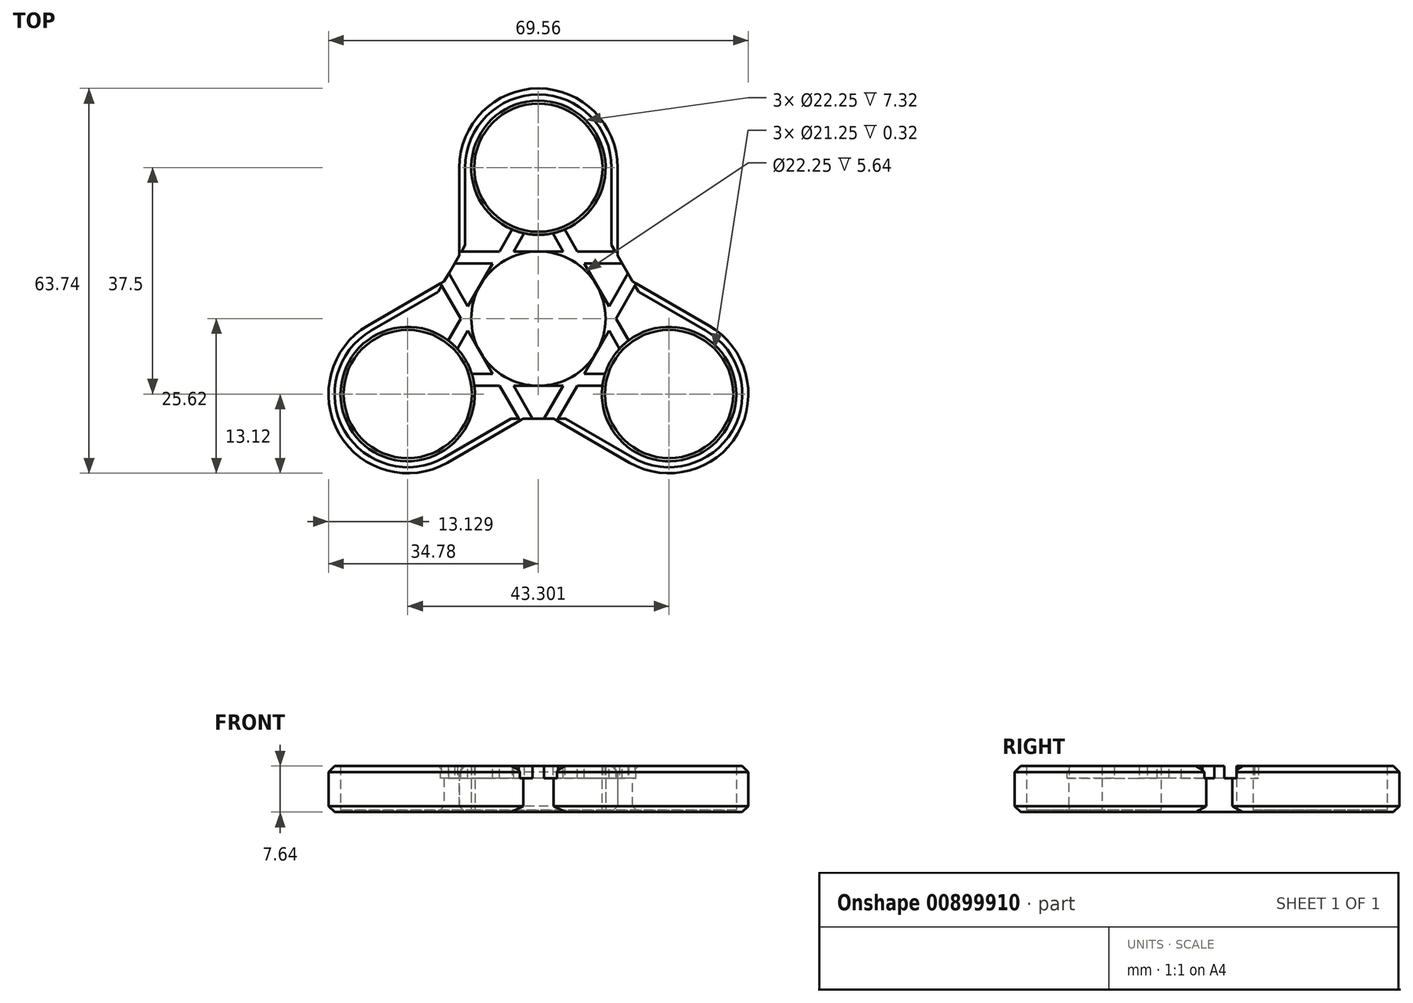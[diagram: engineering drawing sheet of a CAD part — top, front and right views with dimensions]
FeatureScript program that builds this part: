
annotation { "Feature Type Name" : "Feature", "Feature Type Description" : "" }
export const myFeature = defineFeature(function(context is Context, id is Id, definition is map)
    precondition{}
    {
        {
            var Q0;
            Q0=qCreatedBy(makeId("Top.planeOp"),FACE);
            var sketch = newSketch(context, id + "F0", { "sketchPlane" : qUnion([Q0])});
            skCircle(sketch, "E0", {"center": v(0, 0) * mm, "radius": 11.12 * mm});
            skCircle(sketch, "E1", {"center": v(0, 25) * mm, "radius": 11.12 * mm});
            skCircle(sketch, "E2", {"center": v(0, 25) * mm, "radius": 13.12 * mm});
            skCircle(sketch, "E3", {"center": v(0, 0) * mm, "radius": 13.12 * mm});
            skLineSegment(sketch, "E4", {"start": v(-13.12, 0) * mm, "end": v(-13.12, 25) * mm});
            skLineSegment(sketch, "E5", {"start": v(13.12, 0) * mm, "end": v(13.12, 25) * mm});
            skCircle(sketch, "E6.1.0", {"center": v(-21.65, -12.5) * mm, "radius": 11.12 * mm});
            skCircle(sketch, "E6.1.1", {"center": v(-21.65, -12.5) * mm, "radius": 13.12 * mm});
            skLineSegment(sketch, "E6.1.2", {"start": v(6.56, -11.37) * mm, "end": v(-15.09, -23.87) * mm});
            skLineSegment(sketch, "E6.1.3", {"start": v(-6.56, 11.37) * mm, "end": v(-28.21, -1.13) * mm});
            skCircle(sketch, "E6.2.0", {"center": v(21.65, -12.5) * mm, "radius": 11.12 * mm});
            skCircle(sketch, "E6.2.1", {"center": v(21.65, -12.5) * mm, "radius": 13.12 * mm});
            skLineSegment(sketch, "E6.2.2", {"start": v(6.56, 11.37) * mm, "end": v(28.21, -1.13) * mm});
            skLineSegment(sketch, "E6.2.3", {"start": v(-6.56, -11.37) * mm, "end": v(15.09, -23.87) * mm});
            skSolve(sketch);
        }
        {
            var Q0;
            Q0=makeQuery(id+"F0.imprint","IMPRINT",FACE,{"disambiguationData":[TD([[makeQuery(id+"F0.imprint","IMPRINT",EDGE,{"derivedFrom":sQuery(id+"F0.wireOp",EDGE,"E1")}),-1.0]])]});
            var Q1;
            {var subQ0=sQuery(id+"F0.wireOp",EDGE,"E4");var subQ1=sQuery(id+"F0.wireOp",EDGE,"E2");var subQ2=makeQuery(id+"F0.imprint","INTERSECT",VERTEX,{"derivedFrom":[subQ1,subQ0]});Q1=makeQuery(id+"F0.imprint","IMPRINT",FACE,{"disambiguationData":[TD([[makeQuery(id+"F0.imprint","IMPRINT",EDGE,{"disambiguationData":[TD([[subQ2,-1.0]])],"derivedFrom":subQ1}),-1.0]])]});}
            var Q2;
            {var subQ5=sQuery(id+"F0.wireOp",EDGE,"E4");var subQ6=sQuery(id+"F0.wireOp",EDGE,"E3");var subQ7=makeQuery(id+"F0.imprint","INTERSECT",VERTEX,{"derivedFrom":[subQ6,subQ5]});Q2=makeQuery(id+"F0.imprint","IMPRINT",FACE,{"disambiguationData":[TD([[makeQuery(id+"F0.imprint","IMPRINT",EDGE,{"disambiguationData":[TD([[subQ7,-1.0]])],"derivedFrom":subQ6}),-1.0]])]});}
            var Q3;
            Q3=makeQuery(id+"F0.imprint","IMPRINT",FACE,{"disambiguationData":[TD([[makeQuery(id+"F0.imprint","IMPRINT",EDGE,{"derivedFrom":sQuery(id+"F0.wireOp",EDGE,"E6.1.0")}),-1.0]])]});
            var Q4;
            {var subQ5=sQuery(id+"F0.wireOp",EDGE,"E5");var subQ6=sQuery(id+"F0.wireOp",EDGE,"E3");var subQ7=makeQuery(id+"F0.imprint","INTERSECT",VERTEX,{"derivedFrom":[subQ6,subQ5]});Q4=makeQuery(id+"F0.imprint","IMPRINT",FACE,{"disambiguationData":[TD([[makeQuery(id+"F0.imprint","IMPRINT",EDGE,{"disambiguationData":[TD([[subQ7,1.0]])],"derivedFrom":subQ6}),-1.0]])]});}
            var Q5;
            Q5=makeQuery(id+"F0.imprint","IMPRINT",FACE,{"disambiguationData":[TD([[makeQuery(id+"F0.imprint","IMPRINT",EDGE,{"derivedFrom":sQuery(id+"F0.wireOp",EDGE,"E6.2.0")}),-1.0]])]});
            var Q6;
            {var subQ0=sQuery(id+"F0.wireOp",EDGE,"E5");var subQ1=sQuery(id+"F0.wireOp",EDGE,"E3");var subQ2=makeQuery(id+"F0.imprint","INTERSECT",VERTEX,{"derivedFrom":[subQ1,subQ0]});Q6=makeQuery(id+"F0.imprint","IMPRINT",FACE,{"disambiguationData":[TD([[makeQuery(id+"F0.imprint","IMPRINT",EDGE,{"disambiguationData":[TD([[subQ2,-1.0]])],"derivedFrom":subQ1}),-1.0]])]});}
            var Q7;
            {var subQ0=sQuery(id+"F0.wireOp",EDGE,"E6.1.2");var subQ1=sQuery(id+"F0.wireOp",EDGE,"E3");var subQ2=makeQuery(id+"F0.imprint","INTERSECT",VERTEX,{"derivedFrom":[subQ1,subQ0]});Q7=makeQuery(id+"F0.imprint","IMPRINT",FACE,{"disambiguationData":[TD([[makeQuery(id+"F0.imprint","IMPRINT",EDGE,{"disambiguationData":[TD([[subQ2,1.0]])],"derivedFrom":subQ1}),-1.0]])]});}
            var Q8;
            {var subQ0=sQuery(id+"F0.wireOp",EDGE,"E4");var subQ1=sQuery(id+"F0.wireOp",EDGE,"E3");var subQ2=makeQuery(id+"F0.imprint","INTERSECT",VERTEX,{"derivedFrom":[subQ1,subQ0]});Q8=makeQuery(id+"F0.imprint","IMPRINT",FACE,{"disambiguationData":[TD([[makeQuery(id+"F0.imprint","IMPRINT",EDGE,{"disambiguationData":[TD([[subQ2,1.0]])],"derivedFrom":subQ1}),-1.0]])]});}
            var Q9;
            Q9=makeQuery(id+"F0.imprint","IMPRINT",FACE,{"disambiguationData":[TD([[makeQuery(id+"F0.imprint","IMPRINT",EDGE,{"derivedFrom":sQuery(id+"F0.wireOp",EDGE,"E0")}),-1.0]])]});
            var Q10;
            {var subQ0=sQuery(id+"F0.wireOp",EDGE,"E5");var subQ1=sQuery(id+"F0.wireOp",EDGE,"E2");var subQ2=makeQuery(id+"F0.imprint","INTERSECT",VERTEX,{"derivedFrom":[subQ1,subQ0]});Q10=makeQuery(id+"F0.imprint","IMPRINT",FACE,{"disambiguationData":[TD([[makeQuery(id+"F0.imprint","IMPRINT",EDGE,{"disambiguationData":[TD([[subQ2,1.0]])],"derivedFrom":subQ1}),-1.0]])]});}
            var Q11;
            {var subQ0=sQuery(id+"F0.wireOp",EDGE,"E6.1.2");var subQ1=sQuery(id+"F0.wireOp",EDGE,"E3");var subQ2=makeQuery(id+"F0.imprint","INTERSECT",VERTEX,{"derivedFrom":[subQ1,subQ0]});Q11=makeQuery(id+"F0.imprint","IMPRINT",FACE,{"disambiguationData":[TD([[makeQuery(id+"F0.imprint","IMPRINT",EDGE,{"disambiguationData":[TD([[subQ2,-1.0]])],"derivedFrom":subQ1}),-1.0]])]});}
            var Q12;
            {var subQ0=sQuery(id+"F0.wireOp",EDGE,"E6.2.3");var subQ1=sQuery(id+"F0.wireOp",EDGE,"E3");var subQ2=makeQuery(id+"F0.imprint","INTERSECT",VERTEX,{"derivedFrom":[subQ1,subQ0]});Q12=makeQuery(id+"F0.imprint","IMPRINT",FACE,{"disambiguationData":[TD([[makeQuery(id+"F0.imprint","IMPRINT",EDGE,{"disambiguationData":[TD([[subQ2,1.0]])],"derivedFrom":subQ1}),-1.0]])]});}
            var Q13;
            {var subQ0=sQuery(id+"F0.wireOp",EDGE,"E6.2.1");var subQ1=sQuery(id+"F0.wireOp",EDGE,"E3");var subQ2=makeQuery(id+"F0.imprint","INTERSECT",VERTEX,{"disambiguationData":[OD(0.0)],"derivedFrom":[subQ1,subQ0]});Q13=makeQuery(id+"F0.imprint","IMPRINT",FACE,{"disambiguationData":[TD([[makeQuery(id+"F0.imprint","IMPRINT",EDGE,{"disambiguationData":[TD([[subQ2,-1.0]])],"derivedFrom":subQ1}),1.0]])]});}
            var Q14;
            {var subQ0=sQuery(id+"F0.wireOp",EDGE,"E3");var subQ1=sQuery(id+"F0.wireOp",EDGE,"E2");var subQ2=makeQuery(id+"F0.imprint","INTERSECT",VERTEX,{"disambiguationData":[OD(0.0)],"derivedFrom":[subQ1,subQ0]});Q14=makeQuery(id+"F0.imprint","IMPRINT",FACE,{"disambiguationData":[TD([[makeQuery(id+"F0.imprint","IMPRINT",EDGE,{"disambiguationData":[TD([[subQ2,-1.0]])],"derivedFrom":subQ1}),1.0]])]});}
            var Q15;
            {var subQ0=sQuery(id+"F0.wireOp",EDGE,"E6.1.1");var subQ1=sQuery(id+"F0.wireOp",EDGE,"E3");var subQ2=makeQuery(id+"F0.imprint","INTERSECT",VERTEX,{"disambiguationData":[OD(0.0)],"derivedFrom":[subQ1,subQ0]});Q15=makeQuery(id+"F0.imprint","IMPRINT",FACE,{"disambiguationData":[TD([[makeQuery(id+"F0.imprint","IMPRINT",EDGE,{"disambiguationData":[TD([[subQ2,-1.0]])],"derivedFrom":subQ1}),1.0]])]});}
            extrude(context, id + "F1", {"entities" : qUnion([Q0, Q1, Q2, Q3, Q4, Q5, Q6, Q7, Q8, Q9, Q10, Q11, Q12, Q13, Q14, Q15]), "endBound" : BoundingType.SYMMETRIC, "depth" : 7.64 * mm, "offsetDistance" : 25 * mm});
        }
        {
            var Q0;
            Q0=makeQuery(id+"F1.opExtrude","CAP_FACE",FACE,{"disambiguationData":[OSD([sQuery(id+"F0.wireOp",EDGE,"E0"),sQuery(id+"F0.wireOp",EDGE,"E1"),sQuery(id+"F0.wireOp",EDGE,"E2"),sQuery(id+"F0.wireOp",EDGE,"E4"),sQuery(id+"F0.wireOp",EDGE,"E5"),sQuery(id+"F0.wireOp",EDGE,"E6.1.0"),sQuery(id+"F0.wireOp",EDGE,"E6.1.1"),sQuery(id+"F0.wireOp",EDGE,"E6.1.2"),sQuery(id+"F0.wireOp",EDGE,"E6.1.3"),sQuery(id+"F0.wireOp",EDGE,"E6.2.0"),sQuery(id+"F0.wireOp",EDGE,"E6.2.1"),sQuery(id+"F0.wireOp",EDGE,"E6.2.2"),sQuery(id+"F0.wireOp",EDGE,"E6.2.3")])],"isStart":false});
            var sketch = newSketch(context, id + "F2", { "sketchPlane" : qUnion([Q0])});
            skCircle(sketch, "E7.cCircle", {"center": v(0, 0) * mm, "radius": 11.12 * mm, "construction": true});
            skLineSegment(sketch, "E7.0", {"start": v(-19.27, 11.12) * mm, "end": v(19.27, 11.13) * mm});
            skLineSegment(sketch, "E7.1", {"start": v(19.27, 11.13) * mm, "end": v(0, -22.25) * mm});
            skLineSegment(sketch, "E7.2", {"start": v(0, -22.25) * mm, "end": v(-19.27, 11.13) * mm});
            skPoint(sketch, "E7.0.midPoint", {"position": v(0, 11.12) * mm});
            skLineSegment(sketch, "E8.0", {"start": v(0.09, 22.1) * mm, "end": v(19.18, -10.98) * mm});
            skLineSegment(sketch, "E8.1", {"start": v(19.1, -11.13) * mm, "end": v(-19.1, -11.12) * mm});
            skLineSegment(sketch, "E8.2", {"start": v(-19.18, -10.98) * mm, "end": v(-0.09, 22.1) * mm});
            skPoint(sketch, "E8.0.midPoint", {"position": v(9.63, 5.56) * mm});
            skLineSegment(sketch, "E9.0", {"start": v(0, 18.25) * mm, "end": v(15.8, -9.13) * mm});
            skLineSegment(sketch, "E9.1", {"start": v(-15.8, -9.13) * mm, "end": v(0, 18.25) * mm});
            skLineSegment(sketch, "E9.2", {"start": v(15.8, -9.13) * mm, "end": v(-15.8, -9.12) * mm});
            skLineSegment(sketch, "E10.0", {"start": v(15.8, 9.13) * mm, "end": v(0, -18.25) * mm});
            skLineSegment(sketch, "E10.1", {"start": v(-15.8, 9.12) * mm, "end": v(15.8, 9.12) * mm});
            skLineSegment(sketch, "E10.2", {"start": v(0, -18.25) * mm, "end": v(-15.8, 9.13) * mm});
            skPoint(sketch, "E11.visualSharp", {"position": v(19.27, -11.13) * mm});
            skArc(sketch, "E11.filletArc", {"start": v(19.1, -11.13) * mm, "mid": v(19.18, -11.08) * mm, "end": v(19.18, -10.98) * mm});
            skPoint(sketch, "E12.visualSharp", {"position": v(-19.27, -11.12) * mm});
            skArc(sketch, "E12.filletArc", {"start": v(-19.18, -10.97) * mm, "mid": v(-19.18, -11.07) * mm, "end": v(-19.1, -11.12) * mm});
            skPoint(sketch, "E13.visualSharp", {"position": v(0, 22.25) * mm});
            skArc(sketch, "E13.filletArc", {"start": v(0.09, 22.1) * mm, "mid": v(0, 22.15) * mm, "end": v(-0.09, 22.1) * mm});
            skSolve(sketch);
        }
        {
            var Q0;
            Q0=makeQuery(id+"F1.opExtrude","CAP_FACE",FACE,{"disambiguationData":[OSD([sQuery(id+"F0.wireOp",EDGE,"E0"),sQuery(id+"F0.wireOp",EDGE,"E1"),sQuery(id+"F0.wireOp",EDGE,"E2"),sQuery(id+"F0.wireOp",EDGE,"E4"),sQuery(id+"F0.wireOp",EDGE,"E5"),sQuery(id+"F0.wireOp",EDGE,"E6.1.0"),sQuery(id+"F0.wireOp",EDGE,"E6.1.1"),sQuery(id+"F0.wireOp",EDGE,"E6.1.2"),sQuery(id+"F0.wireOp",EDGE,"E6.1.3"),sQuery(id+"F0.wireOp",EDGE,"E6.2.0"),sQuery(id+"F0.wireOp",EDGE,"E6.2.1"),sQuery(id+"F0.wireOp",EDGE,"E6.2.2"),sQuery(id+"F0.wireOp",EDGE,"E6.2.3")])],"isStart":false});
            var sketch = newSketch(context, id + "F3", { "sketchPlane" : qUnion([Q0])});
            skArc(sketch, "E14.0", {"start": v(13.12, 25) * mm, "mid": v(0, 38.12) * mm, "end": v(-13.12, 25) * mm});
            skCircle(sketch, "E15.cCircle", {"center": v(0, 25) * mm, "radius": 13.12 * mm, "construction": true});
            skLineSegment(sketch, "E15.0", {"start": v(13.12, 32.58) * mm, "end": v(13.12, 17.42) * mm});
            skLineSegment(sketch, "E15.1", {"start": v(13.13, 17.42) * mm, "end": v(0, 9.84) * mm});
            skLineSegment(sketch, "E15.2", {"start": v(0, 9.84) * mm, "end": v(-13.13, 17.42) * mm});
            skLineSegment(sketch, "E15.3", {"start": v(-13.13, 17.42) * mm, "end": v(-13.13, 32.58) * mm});
            skLineSegment(sketch, "E15.4", {"start": v(-13.13, 32.58) * mm, "end": v(0, 40.16) * mm});
            skLineSegment(sketch, "E15.5", {"start": v(0, 40.16) * mm, "end": v(13.12, 32.58) * mm});
            skPoint(sketch, "E15.0.midPoint", {"position": v(13.12, 25) * mm});
            skSolve(sketch);
        }
        {
            var Q0;
            Q0=makeQuery(id+"F1.opExtrude","SWEPT_EDGE",EDGE,{"disambiguationData":[OSD([sQuery(id+"F0.wireOp",EDGE,"E5"),sQuery(id+"F0.wireOp",EDGE,"E6.2.2")])]});
            var Q1;
            Q1=makeQuery(id+"F1.opExtrude","SWEPT_EDGE",EDGE,{"disambiguationData":[OSD([sQuery(id+"F0.wireOp",EDGE,"E4"),sQuery(id+"F0.wireOp",EDGE,"E6.1.3")])]});
            var Q2;
            Q2=makeQuery(id+"F1.opExtrude","SWEPT_EDGE",EDGE,{"disambiguationData":[OSD([sQuery(id+"F0.wireOp",EDGE,"E6.1.2"),sQuery(id+"F0.wireOp",EDGE,"E6.2.3")])]});
            chamfer(context, id + "F4", {"entities" : qUnion([Q0, Q1, Q2]), "width" : 5 * mm, "tangentPropagation" : true});
        }
        {
            var Q0;
            Q0=makeQuery(id+"F1.opExtrude","CAP_EDGE",EDGE,{"disambiguationData":[OSD([sQuery(id+"F0.wireOp",EDGE,"E5")])],"isStart":false});
            var Q1;
            Q1=makeQuery(id+"F1.opExtrude","CAP_EDGE",EDGE,{"disambiguationData":[OSD([sQuery(id+"F0.wireOp",EDGE,"E6.2.3")])],"isStart":false});
            var Q2;
            Q2=makeQuery(id+"F1.opExtrude","CAP_EDGE",EDGE,{"disambiguationData":[OSD([sQuery(id+"F0.wireOp",EDGE,"E6.1.3")])],"isStart":false});
            chamfer(context, id + "F5", {"entities" : qUnion([Q0, Q1, Q2]), "width" : 1 * mm, "tangentPropagation" : true});
        }
        {
            var Q0;
            {var subQ0=sQuery(id+"F2.wireOp",EDGE,"E8.2");var subQ12=sQuery(id+"F2.wireOp",EDGE,"E7.2");var subQ13=makeQuery(id+"F2.imprint","INTERSECT",VERTEX,{"derivedFrom":[subQ12,subQ0]});Q0=makeQuery(id+"F2.imprint","IMPRINT",FACE,{"disambiguationData":[TD([[makeQuery(id+"F2.imprint","IMPRINT",EDGE,{"disambiguationData":[TD([[subQ13,-1.0]])],"derivedFrom":subQ0}),1.0]])]});}
            var Q1;
            {var subQ0=sQuery(id+"F2.wireOp",EDGE,"E8.2");var subQ1=sQuery(id+"F2.wireOp",EDGE,"E7.0");var subQ2=makeQuery(id+"F2.imprint","INTERSECT",VERTEX,{"derivedFrom":[subQ1,subQ0]});Q1=makeQuery(id+"F2.imprint","IMPRINT",FACE,{"disambiguationData":[TD([[makeQuery(id+"F2.imprint","IMPRINT",EDGE,{"disambiguationData":[TD([[subQ2,-1.0]])],"derivedFrom":subQ1}),1.0]])]});}
            var Q2;
            {var subQ0=sQuery(id+"F2.wireOp",EDGE,"E8.0");var subQ9=sQuery(id+"F2.wireOp",EDGE,"E7.0");var subQ10=makeQuery(id+"F2.imprint","INTERSECT",VERTEX,{"derivedFrom":[subQ9,subQ0]});Q2=makeQuery(id+"F2.imprint","IMPRINT",FACE,{"disambiguationData":[TD([[makeQuery(id+"F2.imprint","IMPRINT",EDGE,{"disambiguationData":[TD([[subQ10,-1.0]])],"derivedFrom":subQ0}),1.0]])]});}
            var Q3;
            {var subQ1=sQuery(id+"F2.wireOp",EDGE,"E7.1");var subQ7=sQuery(id+"F2.wireOp",EDGE,"E8.0");var subQ8=makeQuery(id+"F2.imprint","INTERSECT",VERTEX,{"derivedFrom":[subQ1,subQ7]});Q3=makeQuery(id+"F2.imprint","IMPRINT",FACE,{"disambiguationData":[TD([[makeQuery(id+"F2.imprint","IMPRINT",EDGE,{"disambiguationData":[TD([[subQ8,-1.0]])],"derivedFrom":subQ1}),1.0]])]});}
            var Q4;
            {var subQ0=sQuery(id+"F2.wireOp",EDGE,"E8.1");var subQ11=sQuery(id+"F2.wireOp",EDGE,"E7.1");var subQ12=makeQuery(id+"F2.imprint","INTERSECT",VERTEX,{"derivedFrom":[subQ11,subQ0]});Q4=makeQuery(id+"F2.imprint","IMPRINT",FACE,{"disambiguationData":[TD([[makeQuery(id+"F2.imprint","IMPRINT",EDGE,{"disambiguationData":[TD([[subQ12,-1.0]])],"derivedFrom":subQ0}),1.0]])]});}
            var Q5;
            {var subQ1=sQuery(id+"F2.wireOp",EDGE,"E7.2");var subQ7=sQuery(id+"F2.wireOp",EDGE,"E8.1");var subQ8=makeQuery(id+"F2.imprint","INTERSECT",VERTEX,{"derivedFrom":[subQ1,subQ7]});Q5=makeQuery(id+"F2.imprint","IMPRINT",FACE,{"disambiguationData":[TD([[makeQuery(id+"F2.imprint","IMPRINT",EDGE,{"disambiguationData":[TD([[subQ8,-1.0]])],"derivedFrom":subQ1}),1.0]])]});}
            var Q6;
            {var subQ1=sQuery(id+"F2.wireOp",EDGE,"E7.1");var subQ5=sQuery(id+"F2.wireOp",EDGE,"E8.0");var subQ6=makeQuery(id+"F2.imprint","INTERSECT",VERTEX,{"derivedFrom":[subQ1,subQ5]});Q6=makeQuery(id+"F2.imprint","IMPRINT",FACE,{"disambiguationData":[TD([[makeQuery(id+"F2.imprint","IMPRINT",EDGE,{"disambiguationData":[TD([[subQ6,-1.0]])],"derivedFrom":subQ1}),-1.0]])]});}
            var Q7;
            {var subQ0=sQuery(id+"F2.wireOp",EDGE,"E9.0");var subQ1=sQuery(id+"F2.wireOp",EDGE,"E7.0");var subQ2=makeQuery(id+"F2.imprint","INTERSECT",VERTEX,{"derivedFrom":[subQ1,subQ0]});Q7=makeQuery(id+"F2.imprint","IMPRINT",FACE,{"disambiguationData":[TD([[makeQuery(id+"F2.imprint","IMPRINT",EDGE,{"disambiguationData":[TD([[subQ2,-1.0]])],"derivedFrom":subQ1}),-1.0]])]});}
            var Q8;
            {var subQ1=sQuery(id+"F2.wireOp",EDGE,"E7.0");var subQ5=sQuery(id+"F2.wireOp",EDGE,"E8.2");var subQ6=makeQuery(id+"F2.imprint","INTERSECT",VERTEX,{"derivedFrom":[subQ1,subQ5]});Q8=makeQuery(id+"F2.imprint","IMPRINT",FACE,{"disambiguationData":[TD([[makeQuery(id+"F2.imprint","IMPRINT",EDGE,{"disambiguationData":[TD([[subQ6,-1.0]])],"derivedFrom":subQ1}),-1.0]])]});}
            var Q9;
            {var subQ5=sQuery(id+"F2.wireOp",EDGE,"E7.2");var subQ7=sQuery(id+"F2.wireOp",EDGE,"E9.1");var subQ8=makeQuery(id+"F2.imprint","INTERSECT",VERTEX,{"derivedFrom":[subQ5,subQ7]});Q9=makeQuery(id+"F2.imprint","IMPRINT",FACE,{"disambiguationData":[TD([[makeQuery(id+"F2.imprint","IMPRINT",EDGE,{"disambiguationData":[TD([[subQ8,-1.0]])],"derivedFrom":subQ5}),-1.0]])]});}
            var Q10;
            {var subQ1=sQuery(id+"F2.wireOp",EDGE,"E8.1");var subQ5=sQuery(id+"F2.wireOp",EDGE,"E7.2");var subQ6=makeQuery(id+"F2.imprint","INTERSECT",VERTEX,{"derivedFrom":[subQ5,subQ1]});Q10=makeQuery(id+"F2.imprint","IMPRINT",FACE,{"disambiguationData":[TD([[makeQuery(id+"F2.imprint","IMPRINT",EDGE,{"disambiguationData":[TD([[subQ6,-1.0]])],"derivedFrom":subQ5}),-1.0]])]});}
            var Q11;
            {var subQ5=sQuery(id+"F2.wireOp",EDGE,"E9.2");var subQ6=sQuery(id+"F2.wireOp",EDGE,"E7.1");var subQ7=makeQuery(id+"F2.imprint","INTERSECT",VERTEX,{"derivedFrom":[subQ6,subQ5]});Q11=makeQuery(id+"F2.imprint","IMPRINT",FACE,{"disambiguationData":[TD([[makeQuery(id+"F2.imprint","IMPRINT",EDGE,{"disambiguationData":[TD([[subQ7,-1.0]])],"derivedFrom":subQ6}),-1.0]])]});}
            var Q12;
            {var subQ0=sQuery(id+"F2.wireOp",EDGE,"E9.0");var subQ1=sQuery(id+"F2.wireOp",EDGE,"E7.0");var subQ2=makeQuery(id+"F2.imprint","INTERSECT",VERTEX,{"derivedFrom":[subQ1,subQ0]});Q12=makeQuery(id+"F2.imprint","IMPRINT",FACE,{"disambiguationData":[TD([[makeQuery(id+"F2.imprint","IMPRINT",EDGE,{"disambiguationData":[TD([[subQ2,1.0]])],"derivedFrom":subQ1}),-1.0]])]});}
            var Q13;
            {var subQ0=sQuery(id+"F2.wireOp",EDGE,"E9.1");var subQ1=sQuery(id+"F2.wireOp",EDGE,"E7.0");var subQ2=makeQuery(id+"F2.imprint","INTERSECT",VERTEX,{"derivedFrom":[subQ1,subQ0]});Q13=makeQuery(id+"F2.imprint","IMPRINT",FACE,{"disambiguationData":[TD([[makeQuery(id+"F2.imprint","IMPRINT",EDGE,{"disambiguationData":[TD([[subQ2,-1.0]])],"derivedFrom":subQ1}),-1.0]])]});}
            var Q14;
            {var subQ0=sQuery(id+"F2.wireOp",EDGE,"E10.1");var subQ1=sQuery(id+"F2.wireOp",EDGE,"E8.2");var subQ2=makeQuery(id+"F2.imprint","INTERSECT",VERTEX,{"derivedFrom":[subQ1,subQ0]});Q14=makeQuery(id+"F2.imprint","IMPRINT",FACE,{"disambiguationData":[TD([[makeQuery(id+"F2.imprint","IMPRINT",EDGE,{"disambiguationData":[TD([[subQ2,1.0]])],"derivedFrom":subQ1}),-1.0]])]});}
            var Q15;
            {var subQ0=sQuery(id+"F2.wireOp",EDGE,"E10.2");var subQ1=sQuery(id+"F2.wireOp",EDGE,"E8.2");var subQ2=makeQuery(id+"F2.imprint","INTERSECT",VERTEX,{"derivedFrom":[subQ1,subQ0]});Q15=makeQuery(id+"F2.imprint","IMPRINT",FACE,{"disambiguationData":[TD([[makeQuery(id+"F2.imprint","IMPRINT",EDGE,{"disambiguationData":[TD([[subQ2,-1.0]])],"derivedFrom":subQ1}),-1.0]])]});}
            var Q16;
            {var subQ0=sQuery(id+"F2.wireOp",EDGE,"E9.1");var subQ1=sQuery(id+"F2.wireOp",EDGE,"E7.2");var subQ2=makeQuery(id+"F2.imprint","INTERSECT",VERTEX,{"derivedFrom":[subQ1,subQ0]});Q16=makeQuery(id+"F2.imprint","IMPRINT",FACE,{"disambiguationData":[TD([[makeQuery(id+"F2.imprint","IMPRINT",EDGE,{"disambiguationData":[TD([[subQ2,1.0]])],"derivedFrom":subQ1}),-1.0]])]});}
            var Q17;
            {var subQ0=sQuery(id+"F2.wireOp",EDGE,"E9.2");var subQ1=sQuery(id+"F2.wireOp",EDGE,"E7.2");var subQ2=makeQuery(id+"F2.imprint","INTERSECT",VERTEX,{"derivedFrom":[subQ1,subQ0]});Q17=makeQuery(id+"F2.imprint","IMPRINT",FACE,{"disambiguationData":[TD([[makeQuery(id+"F2.imprint","IMPRINT",EDGE,{"disambiguationData":[TD([[subQ2,-1.0]])],"derivedFrom":subQ1}),-1.0]])]});}
            var Q18;
            {var subQ0=sQuery(id+"F2.wireOp",EDGE,"E10.0");var subQ1=sQuery(id+"F2.wireOp",EDGE,"E8.1");var subQ2=makeQuery(id+"F2.imprint","INTERSECT",VERTEX,{"derivedFrom":[subQ1,subQ0]});Q18=makeQuery(id+"F2.imprint","IMPRINT",FACE,{"disambiguationData":[TD([[makeQuery(id+"F2.imprint","IMPRINT",EDGE,{"disambiguationData":[TD([[subQ2,-1.0]])],"derivedFrom":subQ1}),-1.0]])]});}
            var Q19;
            {var subQ0=sQuery(id+"F2.wireOp",EDGE,"E10.2");var subQ1=sQuery(id+"F2.wireOp",EDGE,"E8.1");var subQ2=makeQuery(id+"F2.imprint","INTERSECT",VERTEX,{"derivedFrom":[subQ1,subQ0]});Q19=makeQuery(id+"F2.imprint","IMPRINT",FACE,{"disambiguationData":[TD([[makeQuery(id+"F2.imprint","IMPRINT",EDGE,{"disambiguationData":[TD([[subQ2,1.0]])],"derivedFrom":subQ1}),-1.0]])]});}
            var Q20;
            {var subQ0=sQuery(id+"F2.wireOp",EDGE,"E9.2");var subQ1=sQuery(id+"F2.wireOp",EDGE,"E7.1");var subQ2=makeQuery(id+"F2.imprint","INTERSECT",VERTEX,{"derivedFrom":[subQ1,subQ0]});Q20=makeQuery(id+"F2.imprint","IMPRINT",FACE,{"disambiguationData":[TD([[makeQuery(id+"F2.imprint","IMPRINT",EDGE,{"disambiguationData":[TD([[subQ2,1.0]])],"derivedFrom":subQ1}),-1.0]])]});}
            var Q21;
            {var subQ0=sQuery(id+"F2.wireOp",EDGE,"E9.0");var subQ1=sQuery(id+"F2.wireOp",EDGE,"E7.1");var subQ2=makeQuery(id+"F2.imprint","INTERSECT",VERTEX,{"derivedFrom":[subQ1,subQ0]});Q21=makeQuery(id+"F2.imprint","IMPRINT",FACE,{"disambiguationData":[TD([[makeQuery(id+"F2.imprint","IMPRINT",EDGE,{"disambiguationData":[TD([[subQ2,-1.0]])],"derivedFrom":subQ1}),-1.0]])]});}
            var Q22;
            {var subQ0=sQuery(id+"F2.wireOp",EDGE,"E10.0");var subQ1=sQuery(id+"F2.wireOp",EDGE,"E8.0");var subQ2=makeQuery(id+"F2.imprint","INTERSECT",VERTEX,{"derivedFrom":[subQ1,subQ0]});Q22=makeQuery(id+"F2.imprint","IMPRINT",FACE,{"disambiguationData":[TD([[makeQuery(id+"F2.imprint","IMPRINT",EDGE,{"disambiguationData":[TD([[subQ2,1.0]])],"derivedFrom":subQ1}),-1.0]])]});}
            var Q23;
            {var subQ0=sQuery(id+"F2.wireOp",EDGE,"E10.1");var subQ1=sQuery(id+"F2.wireOp",EDGE,"E8.0");var subQ2=makeQuery(id+"F2.imprint","INTERSECT",VERTEX,{"derivedFrom":[subQ1,subQ0]});Q23=makeQuery(id+"F2.imprint","IMPRINT",FACE,{"disambiguationData":[TD([[makeQuery(id+"F2.imprint","IMPRINT",EDGE,{"disambiguationData":[TD([[subQ2,-1.0]])],"derivedFrom":subQ1}),-1.0]])]});}
            var Q24;
            {var subQ4=sQuery(id+"F2.wireOp",EDGE,"E10.1");var subQ5=sQuery(id+"F2.wireOp",EDGE,"E9.0");var subQ6=makeQuery(id+"F2.imprint","INTERSECT",VERTEX,{"derivedFrom":[subQ5,subQ4]});Q24=makeQuery(id+"F2.imprint","IMPRINT",FACE,{"disambiguationData":[TD([[makeQuery(id+"F2.imprint","IMPRINT",EDGE,{"disambiguationData":[TD([[subQ6,-1.0]])],"derivedFrom":subQ5}),1.0]])]});}
            var Q25;
            {var subQ2=sQuery(id+"F2.wireOp",EDGE,"E9.0");var subQ4=sQuery(id+"F2.wireOp",EDGE,"E10.1");var subQ5=makeQuery(id+"F2.imprint","INTERSECT",VERTEX,{"derivedFrom":[subQ2,subQ4]});Q25=makeQuery(id+"F2.imprint","IMPRINT",FACE,{"disambiguationData":[TD([[makeQuery(id+"F2.imprint","IMPRINT",EDGE,{"disambiguationData":[TD([[subQ5,1.0]])],"derivedFrom":subQ2}),-1.0]])]});}
            var Q26;
            {var subQ0=sQuery(id+"F2.wireOp",EDGE,"E10.2");var subQ1=sQuery(id+"F2.wireOp",EDGE,"E9.1");var subQ2=makeQuery(id+"F2.imprint","INTERSECT",VERTEX,{"derivedFrom":[subQ1,subQ0]});Q26=makeQuery(id+"F2.imprint","IMPRINT",FACE,{"disambiguationData":[TD([[makeQuery(id+"F2.imprint","IMPRINT",EDGE,{"disambiguationData":[TD([[subQ2,-1.0]])],"derivedFrom":subQ1}),1.0]])]});}
            var Q27;
            {var subQ0=sQuery(id+"F2.wireOp",EDGE,"E10.2");var subQ1=sQuery(id+"F2.wireOp",EDGE,"E9.1");var subQ2=makeQuery(id+"F2.imprint","INTERSECT",VERTEX,{"derivedFrom":[subQ1,subQ0]});Q27=makeQuery(id+"F2.imprint","IMPRINT",FACE,{"disambiguationData":[TD([[makeQuery(id+"F2.imprint","IMPRINT",EDGE,{"disambiguationData":[TD([[subQ2,1.0]])],"derivedFrom":subQ1}),-1.0]])]});}
            var Q28;
            {var subQ2=sQuery(id+"F2.wireOp",EDGE,"E10.0");var subQ4=sQuery(id+"F2.wireOp",EDGE,"E9.2");var subQ5=makeQuery(id+"F2.imprint","INTERSECT",VERTEX,{"derivedFrom":[subQ4,subQ2]});Q28=makeQuery(id+"F2.imprint","IMPRINT",FACE,{"disambiguationData":[TD([[makeQuery(id+"F2.imprint","IMPRINT",EDGE,{"disambiguationData":[TD([[subQ5,-1.0]])],"derivedFrom":subQ4}),1.0]])]});}
            var Q29;
            {var subQ2=sQuery(id+"F2.wireOp",EDGE,"E9.0");var subQ4=sQuery(id+"F2.wireOp",EDGE,"E10.0");var subQ8=makeQuery(id+"F2.imprint","INTERSECT",VERTEX,{"derivedFrom":[subQ2,subQ4]});Q29=makeQuery(id+"F2.imprint","IMPRINT",FACE,{"disambiguationData":[TD([[makeQuery(id+"F2.imprint","IMPRINT",EDGE,{"disambiguationData":[TD([[subQ8,-1.0]])],"derivedFrom":subQ2}),-1.0]])]});}
            var Q30;
            {var subQ0=sQuery(id+"F2.wireOp",EDGE,"E10.2");var subQ1=sQuery(id+"F2.wireOp",EDGE,"E9.1");var subQ2=makeQuery(id+"F2.imprint","INTERSECT",VERTEX,{"derivedFrom":[subQ1,subQ0]});Q30=makeQuery(id+"F2.imprint","IMPRINT",FACE,{"disambiguationData":[TD([[makeQuery(id+"F2.imprint","IMPRINT",EDGE,{"disambiguationData":[TD([[subQ2,1.0]])],"derivedFrom":subQ1}),1.0]])]});}
            var Q31;
            {var subQ0=sQuery(id+"F2.wireOp",EDGE,"E10.2");var subQ1=sQuery(id+"F2.wireOp",EDGE,"E9.2");var subQ2=makeQuery(id+"F2.imprint","INTERSECT",VERTEX,{"derivedFrom":[subQ1,subQ0]});Q31=makeQuery(id+"F2.imprint","IMPRINT",FACE,{"disambiguationData":[TD([[makeQuery(id+"F2.imprint","IMPRINT",EDGE,{"disambiguationData":[TD([[subQ2,-1.0]])],"derivedFrom":subQ1}),1.0]])]});}
            var Q32;
            {var subQ0=sQuery(id+"F2.wireOp",EDGE,"E10.0");var subQ1=sQuery(id+"F2.wireOp",EDGE,"E9.2");var subQ2=makeQuery(id+"F2.imprint","INTERSECT",VERTEX,{"derivedFrom":[subQ1,subQ0]});Q32=makeQuery(id+"F2.imprint","IMPRINT",FACE,{"disambiguationData":[TD([[makeQuery(id+"F2.imprint","IMPRINT",EDGE,{"disambiguationData":[TD([[subQ2,1.0]])],"derivedFrom":subQ1}),1.0]])]});}
            var Q33;
            {var subQ0=sQuery(id+"F2.wireOp",EDGE,"E10.0");var subQ1=sQuery(id+"F2.wireOp",EDGE,"E9.0");var subQ2=makeQuery(id+"F2.imprint","INTERSECT",VERTEX,{"derivedFrom":[subQ1,subQ0]});Q33=makeQuery(id+"F2.imprint","IMPRINT",FACE,{"disambiguationData":[TD([[makeQuery(id+"F2.imprint","IMPRINT",EDGE,{"disambiguationData":[TD([[subQ2,-1.0]])],"derivedFrom":subQ1}),1.0]])]});}
            var Q34;
            {var subQ0=sQuery(id+"F2.wireOp",EDGE,"E10.1");var subQ1=sQuery(id+"F2.wireOp",EDGE,"E9.0");var subQ2=makeQuery(id+"F2.imprint","INTERSECT",VERTEX,{"derivedFrom":[subQ1,subQ0]});Q34=makeQuery(id+"F2.imprint","IMPRINT",FACE,{"disambiguationData":[TD([[makeQuery(id+"F2.imprint","IMPRINT",EDGE,{"disambiguationData":[TD([[subQ2,1.0]])],"derivedFrom":subQ1}),1.0]])]});}
            var Q35;
            {var subQ0=sQuery(id+"F2.wireOp",EDGE,"E10.1");var subQ1=sQuery(id+"F2.wireOp",EDGE,"E9.1");var subQ2=makeQuery(id+"F2.imprint","INTERSECT",VERTEX,{"derivedFrom":[subQ1,subQ0]});Q35=makeQuery(id+"F2.imprint","IMPRINT",FACE,{"disambiguationData":[TD([[makeQuery(id+"F2.imprint","IMPRINT",EDGE,{"disambiguationData":[TD([[subQ2,-1.0]])],"derivedFrom":subQ1}),1.0]])]});}
            var Q36;
            {var subQ0=sQuery(id+"F2.wireOp",EDGE,"E9.0");var subQ1=sQuery(id+"F2.wireOp",EDGE,"E7.0");var subQ2=makeQuery(id+"F2.imprint","INTERSECT",VERTEX,{"derivedFrom":[subQ1,subQ0]});Q36=makeQuery(id+"F2.imprint","IMPRINT",FACE,{"disambiguationData":[TD([[makeQuery(id+"F2.imprint","IMPRINT",EDGE,{"disambiguationData":[TD([[subQ2,-1.0]])],"derivedFrom":subQ1}),1.0]])]});}
            var Q37;
            {var subQ0=sQuery(id+"F2.wireOp",EDGE,"E9.2");var subQ1=sQuery(id+"F2.wireOp",EDGE,"E7.1");var subQ2=makeQuery(id+"F2.imprint","INTERSECT",VERTEX,{"derivedFrom":[subQ1,subQ0]});Q37=makeQuery(id+"F2.imprint","IMPRINT",FACE,{"disambiguationData":[TD([[makeQuery(id+"F2.imprint","IMPRINT",EDGE,{"disambiguationData":[TD([[subQ2,-1.0]])],"derivedFrom":subQ1}),1.0]])]});}
            var Q38;
            {var subQ0=sQuery(id+"F2.wireOp",EDGE,"E8.1");var subQ1=sQuery(id+"F2.wireOp",EDGE,"E7.2");var subQ2=makeQuery(id+"F2.imprint","INTERSECT",VERTEX,{"derivedFrom":[subQ1,subQ0]});Q38=makeQuery(id+"F2.imprint","IMPRINT",FACE,{"disambiguationData":[TD([[makeQuery(id+"F2.imprint","IMPRINT",EDGE,{"disambiguationData":[TD([[subQ2,1.0]])],"derivedFrom":subQ1}),-1.0]])]});}
            var Q39;
            {var subQ0=sQuery(id+"F2.wireOp",EDGE,"E9.1");var subQ1=sQuery(id+"F2.wireOp",EDGE,"E7.2");var subQ2=makeQuery(id+"F2.imprint","INTERSECT",VERTEX,{"derivedFrom":[subQ1,subQ0]});Q39=makeQuery(id+"F2.imprint","IMPRINT",FACE,{"disambiguationData":[TD([[makeQuery(id+"F2.imprint","IMPRINT",EDGE,{"disambiguationData":[TD([[subQ2,-1.0]])],"derivedFrom":subQ1}),1.0]])]});}
            var Q40;
            {var subQ0=sQuery(id+"F2.wireOp",EDGE,"E8.2");var subQ1=sQuery(id+"F2.wireOp",EDGE,"E7.0");var subQ2=makeQuery(id+"F2.imprint","INTERSECT",VERTEX,{"derivedFrom":[subQ1,subQ0]});Q40=makeQuery(id+"F2.imprint","IMPRINT",FACE,{"disambiguationData":[TD([[makeQuery(id+"F2.imprint","IMPRINT",EDGE,{"disambiguationData":[TD([[subQ2,1.0]])],"derivedFrom":subQ1}),-1.0]])]});}
            var Q41;
            {var subQ0=sQuery(id+"F2.wireOp",EDGE,"E8.0");var subQ1=sQuery(id+"F2.wireOp",EDGE,"E7.1");var subQ2=makeQuery(id+"F2.imprint","INTERSECT",VERTEX,{"derivedFrom":[subQ1,subQ0]});Q41=makeQuery(id+"F2.imprint","IMPRINT",FACE,{"disambiguationData":[TD([[makeQuery(id+"F2.imprint","IMPRINT",EDGE,{"disambiguationData":[TD([[subQ2,1.0]])],"derivedFrom":subQ1}),-1.0]])]});}
            var Q42;
            {var subQ7=sQuery(id+"F2.wireOp",EDGE,"E7.2");var subQ8=sQuery(id+"F2.wireOp",EDGE,"E7.1");var subQ9=makeQuery(id+"F2.imprint","INTERSECT",VERTEX,{"derivedFrom":[subQ8,subQ7]});Q42=makeQuery(id+"F2.imprint","IMPRINT",FACE,{"disambiguationData":[TD([[makeQuery(id+"F2.imprint","IMPRINT",EDGE,{"disambiguationData":[TD([[subQ9,1.0]])],"derivedFrom":subQ8}),-1.0]])]});}
            var Q43;
            {var subQ4=sQuery(id+"F2.wireOp",EDGE,"E11.filletArc");Q43=makeQuery(id+"F2.imprint","IMPRINT",FACE,{"disambiguationData":[TD([[makeQuery(id+"F2.imprint","IMPRINT",EDGE,{"derivedFrom":subQ4}),1.0]])]});}
            var Q44;
            {var subQ5=sQuery(id+"F2.wireOp",EDGE,"E7.0");var subQ7=sQuery(id+"F2.wireOp",EDGE,"E7.1");var subQ11=makeQuery(id+"F2.imprint","INTERSECT",VERTEX,{"derivedFrom":[subQ5,subQ7]});Q44=makeQuery(id+"F2.imprint","IMPRINT",FACE,{"disambiguationData":[TD([[makeQuery(id+"F2.imprint","IMPRINT",EDGE,{"disambiguationData":[TD([[subQ11,1.0]])],"derivedFrom":subQ5}),-1.0]])]});}
            var Q45;
            {var subQ4=sQuery(id+"F2.wireOp",EDGE,"E13.filletArc");Q45=makeQuery(id+"F2.imprint","IMPRINT",FACE,{"disambiguationData":[TD([[makeQuery(id+"F2.imprint","IMPRINT",EDGE,{"derivedFrom":subQ4}),1.0]])]});}
            var Q46;
            {var subQ5=sQuery(id+"F2.wireOp",EDGE,"E7.2");var subQ6=sQuery(id+"F2.wireOp",EDGE,"E7.0");var subQ7=makeQuery(id+"F2.imprint","INTERSECT",VERTEX,{"derivedFrom":[subQ6,subQ5]});Q46=makeQuery(id+"F2.imprint","IMPRINT",FACE,{"disambiguationData":[TD([[makeQuery(id+"F2.imprint","IMPRINT",EDGE,{"disambiguationData":[TD([[subQ7,-1.0]])],"derivedFrom":subQ6}),-1.0]])]});}
            var Q47;
            {var subQ4=sQuery(id+"F2.wireOp",EDGE,"E12.filletArc");Q47=makeQuery(id+"F2.imprint","IMPRINT",FACE,{"disambiguationData":[TD([[makeQuery(id+"F2.imprint","IMPRINT",EDGE,{"derivedFrom":subQ4}),1.0]])]});}
            extrude(context, id + "F6", {"entities" : qUnion([Q0, Q1, Q2, Q3, Q4, Q5, Q6, Q7, Q8, Q9, Q10, Q11, Q12, Q13, Q14, Q15, Q16, Q17, Q18, Q19, Q20, Q21, Q22, Q23, Q24, Q25, Q26, Q27, Q28, Q29, Q30, Q31, Q32, Q33, Q34, Q35, Q36, Q37, Q38, Q39, Q40, Q41, Q42, Q43, Q44, Q45, Q46, Q47]), "operationType" : NewBodyOperationType.REMOVE, "oppositeDirection" : true, "depth" : 2 * mm, "offsetDistance" : 25 * mm});
        }
        {
            var Q0;
            Q0=makeQuery(id+"F1.opExtrude","CAP_EDGE",EDGE,{"disambiguationData":[OSD([sQuery(id+"F0.wireOp",EDGE,"E6.2.2")])],"isStart":true});
            var Q1;
            Q1=makeQuery(id+"F1.opExtrude","CAP_EDGE",EDGE,{"disambiguationData":[OSD([sQuery(id+"F0.wireOp",EDGE,"E5")])],"isStart":true});
            var Q2;
            Q2=makeQuery(id+"F1.opExtrude","CAP_EDGE",EDGE,{"disambiguationData":[OSD([sQuery(id+"F0.wireOp",EDGE,"E6.1.2")])],"isStart":true});
            chamfer(context, id + "F7", {"entities" : qUnion([Q0, Q1, Q2]), "width" : 1 * mm, "tangentPropagation" : true});
        }
        {
            var Q0;
            Q0=makeQuery(id+"F1.opExtrude","CAP_FACE",FACE,{"disambiguationData":[OSD([sQuery(id+"F0.wireOp",EDGE,"E0"),sQuery(id+"F0.wireOp",EDGE,"E1"),sQuery(id+"F0.wireOp",EDGE,"E2"),sQuery(id+"F0.wireOp",EDGE,"E4"),sQuery(id+"F0.wireOp",EDGE,"E5"),sQuery(id+"F0.wireOp",EDGE,"E6.1.0"),sQuery(id+"F0.wireOp",EDGE,"E6.1.1"),sQuery(id+"F0.wireOp",EDGE,"E6.1.2"),sQuery(id+"F0.wireOp",EDGE,"E6.1.3"),sQuery(id+"F0.wireOp",EDGE,"E6.2.0"),sQuery(id+"F0.wireOp",EDGE,"E6.2.1"),sQuery(id+"F0.wireOp",EDGE,"E6.2.2"),sQuery(id+"F0.wireOp",EDGE,"E6.2.3")])],"isStart":true});
            var sketch = newSketch(context, id + "F8", { "sketchPlane" : qUnion([Q0])});
            skCircle(sketch, "E16.0", {"center": v(-21.65, 12.5) * mm, "radius": 11.13 * mm});
            skCircle(sketch, "E17.0", {"center": v(21.65, 12.5) * mm, "radius": 11.13 * mm});
            skCircle(sketch, "E18.0", {"center": v(0, -25) * mm, "radius": 11.12 * mm});
            skCircle(sketch, "E19", {"center": v(-21.65, 12.5) * mm, "radius": 10.62 * mm});
            skCircle(sketch, "E20.1.0", {"center": v(0, -25) * mm, "radius": 10.62 * mm});
            skCircle(sketch, "E20.2.0", {"center": v(21.65, 12.5) * mm, "radius": 10.62 * mm});
            skPoint(sketch, "E20.center", {"position": v(0, 0) * mm});
            skSolve(sketch);
        }
        {
            var Q0;
            Q0=makeQuery(id+"F8.imprint","IMPRINT",FACE,{"disambiguationData":[TD([[makeQuery(id+"F8.imprint","IMPRINT",EDGE,{"derivedFrom":sQuery(id+"F8.wireOp",EDGE,"E16.0")}),-1.0]])]});
            var Q1;
            Q1=makeQuery(id+"F8.imprint","IMPRINT",FACE,{"disambiguationData":[TD([[makeQuery(id+"F8.imprint","IMPRINT",EDGE,{"derivedFrom":sQuery(id+"F8.wireOp",EDGE,"E17.0")}),-1.0]])]});
            var Q2;
            Q2=makeQuery(id+"F8.imprint","IMPRINT",FACE,{"disambiguationData":[TD([[makeQuery(id+"F8.imprint","IMPRINT",EDGE,{"derivedFrom":sQuery(id+"F8.wireOp",EDGE,"E18.0")}),-1.0]])]});
            extrude(context, id + "F9", {"entities" : qUnion([Q0, Q1, Q2]), "operationType" : NewBodyOperationType.ADD, "oppositeDirection" : true, "depth" : .32 * mm, "offsetDistance" : 25 * mm});
        }
        {
            var Q0;
            {var subQ13=sQuery(id+"F0.wireOp",EDGE,"E6.2.3");var subQ16=sQuery(id+"F0.wireOp",EDGE,"E6.2.2");var subQ17=sQuery(id+"F0.wireOp",EDGE,"E5");var subQ18=sQuery(id+"F0.wireOp",EDGE,"E4");var subQ19=sQuery(id+"F0.wireOp",EDGE,"E2");var subQ20=sQuery(id+"F0.wireOp",EDGE,"E1");var subQ21=sQuery(id+"F0.wireOp",EDGE,"E6.1.0");var subQ23=sQuery(id+"F0.wireOp",EDGE,"E6.1.2");var subQ24=sQuery(id+"F0.wireOp",EDGE,"E6.1.1");var subQ25=sQuery(id+"F0.wireOp",EDGE,"E6.1.3");var subQ27=sQuery(id+"F0.wireOp",EDGE,"E6.2.0");var subQ28=sQuery(id+"F0.wireOp",EDGE,"E6.2.1");Q0=makeQuery(id+"F6.boolean.opBoolean","SPLIT",FACE,{"disambiguationData":[TD([makeQuery(id+"F1.opExtrude","SWEPT_FACE",FACE,{"disambiguationData":[OSD([subQ20])]})])],"derivedFrom":makeQuery(id+"F1.opExtrude","CAP_FACE",FACE,{"disambiguationData":[OSD([sQuery(id+"F0.wireOp",EDGE,"E0"),subQ20,subQ19,subQ18,subQ17,subQ21,subQ24,subQ23,subQ25,subQ27,subQ28,subQ16,subQ13])],"isStart":false})});}
            var sketch = newSketch(context, id + "F10", { "sketchPlane" : qUnion([Q0])});
            skLineSegment(sketch, "E21", {"start": v(-7.39, 13.01) * mm, "end": v(-3.37, 19.98) * mm});
            skLineSegment(sketch, "E22", {"start": v(-3.37, 19.98) * mm, "end": v(-11.4, 19.98) * mm});
            skLineSegment(sketch, "E23", {"start": v(-11.4, 19.98) * mm, "end": v(-15.43, 13.01) * mm});
            skLineSegment(sketch, "E24", {"start": v(-15.43, 13.01) * mm, "end": v(-7.39, 13.01) * mm});
            skLineSegment(sketch, "E25.1.0", {"start": v(-18.99, 7.07) * mm, "end": v(-23, 0.1) * mm});
            skLineSegment(sketch, "E25.1.1", {"start": v(-23, 0.1) * mm, "end": v(-18.99, -6.85) * mm});
            skLineSegment(sketch, "E25.1.2", {"start": v(-18.99, -6.85) * mm, "end": v(-14.97, 0.1) * mm});
            skLineSegment(sketch, "E25.1.3", {"start": v(-14.97, 0.1) * mm, "end": v(-18.99, 7.07) * mm});
            skLineSegment(sketch, "E25.2.0", {"start": v(-15.62, -12.9) * mm, "end": v(-11.6, -19.87) * mm});
            skLineSegment(sketch, "E25.2.1", {"start": v(-11.6, -19.87) * mm, "end": v(-3.56, -19.87) * mm});
            skLineSegment(sketch, "E25.2.2", {"start": v(-3.56, -19.87) * mm, "end": v(-7.58, -12.9) * mm});
            skLineSegment(sketch, "E25.2.3", {"start": v(-7.58, -12.9) * mm, "end": v(-15.62, -12.9) * mm});
            skLineSegment(sketch, "E25.3.0", {"start": v(3.37, -19.98) * mm, "end": v(11.4, -19.98) * mm});
            skLineSegment(sketch, "E25.3.1", {"start": v(11.4, -19.98) * mm, "end": v(15.43, -13.01) * mm});
            skLineSegment(sketch, "E25.3.2", {"start": v(15.43, -13.01) * mm, "end": v(7.39, -13.01) * mm});
            skLineSegment(sketch, "E25.3.3", {"start": v(7.39, -13.01) * mm, "end": v(3.37, -19.98) * mm});
            skLineSegment(sketch, "E25.4.0", {"start": v(18.99, -7.07) * mm, "end": v(23, -0.1) * mm});
            skLineSegment(sketch, "E25.4.1", {"start": v(23, -0.1) * mm, "end": v(18.99, 6.85) * mm});
            skLineSegment(sketch, "E25.4.2", {"start": v(18.99, 6.85) * mm, "end": v(14.97, -0.1) * mm});
            skLineSegment(sketch, "E25.4.3", {"start": v(14.97, -0.1) * mm, "end": v(18.99, -7.07) * mm});
            skLineSegment(sketch, "E25.5.0", {"start": v(15.62, 12.9) * mm, "end": v(11.6, 19.87) * mm});
            skLineSegment(sketch, "E25.5.1", {"start": v(11.6, 19.87) * mm, "end": v(3.56, 19.87) * mm});
            skLineSegment(sketch, "E25.5.2", {"start": v(3.56, 19.87) * mm, "end": v(7.58, 12.9) * mm});
            skLineSegment(sketch, "E25.5.3", {"start": v(7.58, 12.9) * mm, "end": v(15.62, 12.9) * mm});
            skPoint(sketch, "E25.center", {"position": v(0, 0) * mm});
            skSolve(sketch);
        }
    });
